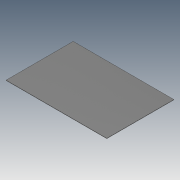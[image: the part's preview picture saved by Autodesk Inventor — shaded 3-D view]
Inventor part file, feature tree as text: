
AUTODESK INVENTOR PART (.ipt)
format: ipt  version: 2020 (Build 240168000, 168)  size: 78,336 bytes
history: native  units: mm
features: other x1, extrude x1, sketch x1
ambient origin geometry x8: Origin, YZ Plane, XZ Plane, XY Plane, X Axis, Y Axis, Z Axis, Center Point
bodies: Body1 (feature_tree)
feature tree (3):
  other  "ソリッド1"
  extrude  "押し出し1"  Depth=500.0mm
  sketch  "スケッチ1"
